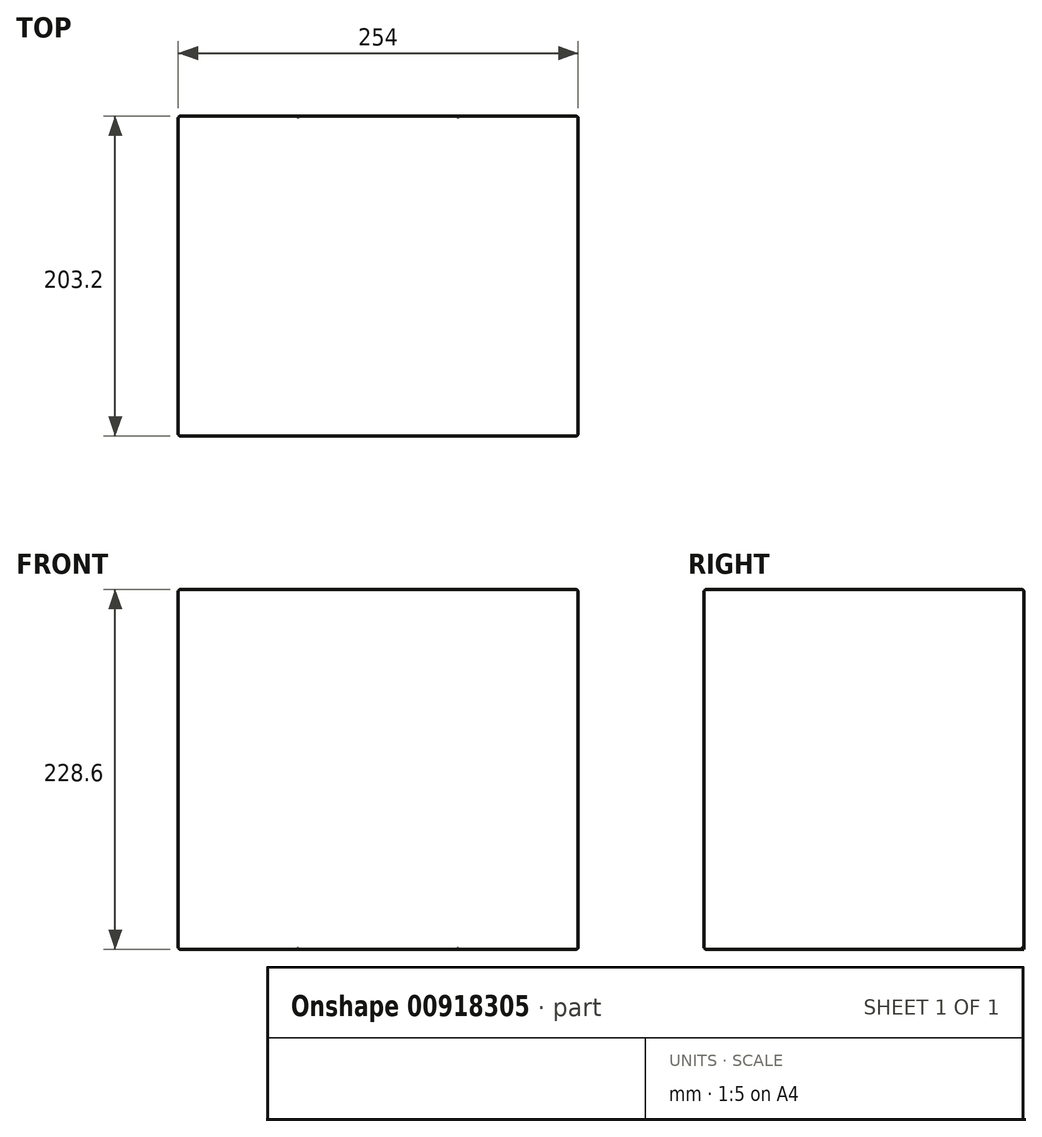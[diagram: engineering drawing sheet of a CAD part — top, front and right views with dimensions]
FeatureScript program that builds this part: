
annotation { "Feature Type Name" : "Feature", "Feature Type Description" : "" }
export const myFeature = defineFeature(function(context is Context, id is Id, definition is map)
    precondition{}
    {
        {
            var Q0;
            Q0=qCreatedBy(makeId("Front.planeOp"),FACE);
            var sketch = newSketch(context, id + "F0", { "sketchPlane" : qUnion([Q0])});
            skLineSegment(sketch, "E0.bottom", {"start": v(127, 114.3) * mm, "end": v(-127, 114.3) * mm});
            skLineSegment(sketch, "E0.top", {"start": v(127, -114.3) * mm, "end": v(-127, -114.3) * mm});
            skLineSegment(sketch, "E0.left", {"start": v(127, 114.3) * mm, "end": v(127, -114.3) * mm});
            skLineSegment(sketch, "E0.right", {"start": v(-127, 114.3) * mm, "end": v(-127, -114.3) * mm});
            skPoint(sketch, "E0.middle", {"position": v(0, 0) * mm});
            skSolve(sketch);
        }
        {
            var Q0;
            Q0=makeQuery(id+"F0.imprint","IMPRINT",FACE,{"disambiguationData":[TD([[makeQuery(id+"F0.imprint","IMPRINT",EDGE,{"derivedFrom":sQuery(id+"F0.wireOp",EDGE,"E0.bottom")}),1.0]])]});
            extrude(context, id + "F1", {"entities" : qUnion([Q0]), "endBound" : BoundingType.SYMMETRIC, "depth" : 203.2 * mm, "offsetDistance" : 25.4 * mm});
        }
        {
            var Q0;
            Q0=makeQuery(id+"F1.opExtrude","SWEPT_FACE",FACE,{"disambiguationData":[OSD([sQuery(id+"F0.wireOp",EDGE,"E0.top")])]});
            var sketch = newSketch(context, id + "F2", { "sketchPlane" : qUnion([Q0])});
            skLineSegment(sketch, "E1.bottom", {"start": v(127, -101.6) * mm, "end": v(50.8, -101.6) * mm});
            skLineSegment(sketch, "E1.top", {"start": v(127, 0) * mm, "end": v(50.8, 0) * mm});
            skLineSegment(sketch, "E1.left", {"start": v(127, -101.6) * mm, "end": v(127, 0) * mm});
            skLineSegment(sketch, "E1.right", {"start": v(50.8, -101.6) * mm, "end": v(50.8, 0) * mm});
            skLineSegment(sketch, "E2", {"start": v(0, -101.6) * mm, "end": v(0, 101.6) * mm, "construction": true});
            skLineSegment(sketch, "E3.MirrorCS", {"start": v(-127, 0) * mm, "end": v(-50.8, 0) * mm});
            skLineSegment(sketch, "E4.MirrorCS", {"start": v(-127, -101.6) * mm, "end": v(-127, 0) * mm});
            skLineSegment(sketch, "E5.MirrorCS", {"start": v(-50.8, -101.6) * mm, "end": v(-50.8, 0) * mm});
            skLineSegment(sketch, "E6.MirrorCS", {"start": v(-127, -101.6) * mm, "end": v(-50.8, -101.6) * mm});
            skSolve(sketch);
        }
        {
            var Q0;
            Q0=makeQuery(id+"F2.imprint","IMPRINT",FACE,{"disambiguationData":[TD([[makeQuery(id+"F2.imprint","IMPRINT",EDGE,{"derivedFrom":sQuery(id+"F2.wireOp",EDGE,"E1.bottom")}),-1.0]])]});
            var Q1;
            Q1=makeQuery(id+"F2.imprint","IMPRINT",FACE,{"disambiguationData":[TD([[makeQuery(id+"F2.imprint","IMPRINT",EDGE,{"derivedFrom":sQuery(id+"F2.wireOp",EDGE,"E3.MirrorCS")}),-1.0]])]});
            extrude(context, id + "F3", {"entities" : qUnion([Q0, Q1]), "operationType" : NewBodyOperationType.REMOVE, "oppositeDirection" : true, "depth" : 25.4 * mm, "offsetDistance" : 25.4 * mm});
        }
        {
            var Q0;
            Q0=makeQuery(id+"F3.boolean.opBoolean","COPY",FACE,{"derivedFrom":makeQuery(id+"F3.opExtrude","CAP_FACE",FACE,{"disambiguationData":[OSD([sQuery(id+"F2.wireOp",EDGE,"E1.bottom"),sQuery(id+"F2.wireOp",EDGE,"E1.top"),sQuery(id+"F2.wireOp",EDGE,"E1.left"),sQuery(id+"F2.wireOp",EDGE,"E1.right")])],"isStart":false})});
            var Q1;
            Q1=makeQuery(id+"F3.boolean.opBoolean","COPY",FACE,{"derivedFrom":makeQuery(id+"F3.opExtrude","CAP_FACE",FACE,{"disambiguationData":[OSD([sQuery(id+"F2.wireOp",EDGE,"E3.MirrorCS"),sQuery(id+"F2.wireOp",EDGE,"E4.MirrorCS"),sQuery(id+"F2.wireOp",EDGE,"E5.MirrorCS"),sQuery(id+"F2.wireOp",EDGE,"E6.MirrorCS")])],"isStart":false})});
            extrude(context, id + "F4", {"entities" : qUnion([Q0, Q1]), "depth" : 25.4 * mm, "offsetDistance" : 25.4 * mm});
        }
        {
            var Q0;
            Q0=makeQuery(id+"F1.opExtrude","CAP_FACE",FACE,{"disambiguationData":[OSD([sQuery(id+"F0.wireOp",EDGE,"E0.bottom"),sQuery(id+"F0.wireOp",EDGE,"E0.top"),sQuery(id+"F0.wireOp",EDGE,"E0.left"),sQuery(id+"F0.wireOp",EDGE,"E0.right")])],"isStart":false});
            var Q1;
            Q1=makeQuery(id+"F1.opExtrude","SWEPT_FACE",FACE,{"disambiguationData":[OSD([sQuery(id+"F0.wireOp",EDGE,"E0.bottom")])]});
            var Q2;
            Q2=makeQuery(id+"F1.opExtrude","CAP_EDGE",EDGE,{"disambiguationData":[OSD([sQuery(id+"F0.wireOp",EDGE,"E0.left")])],"isStart":true});
            var Q3;
            Q3=makeQuery(id+"F4.opExtrude","SWEPT_EDGE",EDGE,{"disambiguationData":[OSD([sQuery(id+"F2.wireOp",EDGE,"E1.bottom"),sQuery(id+"F2.wireOp",EDGE,"E1.left")])]});
            var Q4;
            Q4=makeQuery(id+"F1.opExtrude","CAP_EDGE",EDGE,{"disambiguationData":[OSD([sQuery(id+"F0.wireOp",EDGE,"E0.right")])],"isStart":true});
            var Q5;
            Q5=makeQuery(id+"F4.opExtrude","SWEPT_EDGE",EDGE,{"disambiguationData":[OSD([sQuery(id+"F2.wireOp",EDGE,"E4.MirrorCS"),sQuery(id+"F2.wireOp",EDGE,"E6.MirrorCS")])]});
            var Q6;
            Q6=makeQuery(id+"F1.opExtrude","SWEPT_EDGE",EDGE,{"disambiguationData":[OSD([sQuery(id+"F0.wireOp",EDGE,"E0.top"),sQuery(id+"F0.wireOp",EDGE,"E0.right")])]});
            var Q7;
            Q7=makeQuery(id+"F4.opExtrude","CAP_EDGE",EDGE,{"disambiguationData":[OSD([sQuery(id+"F2.wireOp",EDGE,"E4.MirrorCS")])],"isStart":false});
            var Q8;
            Q8=makeQuery(id+"F4.opExtrude","CAP_EDGE",EDGE,{"disambiguationData":[OSD([sQuery(id+"F2.wireOp",EDGE,"E6.MirrorCS")])],"isStart":false});
            var Q9;
            Q9=makeQuery(id+"F1.opExtrude","CAP_EDGE",EDGE,{"disambiguationData":[OSD([sQuery(id+"F0.wireOp",EDGE,"E0.top")])],"isStart":true});
            var Q10;
            Q10=makeQuery(id+"F4.opExtrude","CAP_EDGE",EDGE,{"disambiguationData":[OSD([sQuery(id+"F2.wireOp",EDGE,"E1.bottom")])],"isStart":false});
            var Q11;
            Q11=makeQuery(id+"F4.opExtrude","CAP_EDGE",EDGE,{"disambiguationData":[OSD([sQuery(id+"F2.wireOp",EDGE,"E1.left")])],"isStart":false});
            var Q12;
            Q12=makeQuery(id+"F1.opExtrude","SWEPT_EDGE",EDGE,{"disambiguationData":[OSD([sQuery(id+"F0.wireOp",EDGE,"E0.top"),sQuery(id+"F0.wireOp",EDGE,"E0.left")])]});
            fillet(context, id + "F5", {"entities" : qUnion([Q0, Q1, Q2, Q3, Q4, Q5, Q6, Q7, Q8, Q9, Q10, Q11, Q12]), "radius" : 1.52 * mm, "tangentPropagation" : true, "allowEdgeOverflow" : false});
        }
        {
            var Q0;
            Q0=makeQuery(id+"F1.opExtrude","SWEPT_FACE",FACE,{"disambiguationData":[OSD([sQuery(id+"F0.wireOp",EDGE,"E0.left")])]});
            var sketch = newSketch(context, id + "F6", { "sketchPlane" : qUnion([Q0])});
            skLineSegment(sketch, "E7.bottom", {"start": v(100.08, -88.9) * mm, "end": v(23.88, -88.9) * mm});
            skLineSegment(sketch, "E7.top", {"start": v(100.08, -63.5) * mm, "end": v(23.88, -63.5) * mm});
            skLineSegment(sketch, "E7.left", {"start": v(100.08, -88.9) * mm, "end": v(100.08, -63.5) * mm});
            skLineSegment(sketch, "E7.right", {"start": v(23.88, -88.9) * mm, "end": v(23.88, -63.5) * mm});
            skSolve(sketch);
        }
        {
            var Q0;
            Q0=makeQuery(id+"F6.imprint","IMPRINT",FACE,{"disambiguationData":[TD([[makeQuery(id+"F6.imprint","IMPRINT",EDGE,{"derivedFrom":sQuery(id+"F6.wireOp",EDGE,"E7.bottom")}),1.0]])]});
            extrude(context, id + "F7", {"entities" : qUnion([Q0]), "operationType" : NewBodyOperationType.REMOVE, "oppositeDirection" : true, "depth" : 25.4 * mm, "offsetDistance" : 25.4 * mm});
        }
        {
            var Q0;
            Q0=makeQuery(id+"F7.boolean.opBoolean","COPY",FACE,{"derivedFrom":makeQuery(id+"F7.opExtrude","CAP_FACE",FACE,{"disambiguationData":[OSD([sQuery(id+"F6.wireOp",EDGE,"E7.bottom"),sQuery(id+"F6.wireOp",EDGE,"E7.top"),sQuery(id+"F6.wireOp",EDGE,"E7.left"),sQuery(id+"F6.wireOp",EDGE,"E7.right")])],"isStart":false})});
            extrude(context, id + "F8", {"entities" : qUnion([Q0]), "operationType" : NewBodyOperationType.ADD, "depth" : 25.4 * mm, "offsetDistance" : 25.4 * mm});
        }
        {
            var Q0;
            Q0=makeQuery(id+"F1.opExtrude","SWEPT_FACE",FACE,{"disambiguationData":[OSD([sQuery(id+"F0.wireOp",EDGE,"E0.right")])]});
            var sketch = newSketch(context, id + "F9", { "sketchPlane" : qUnion([Q0])});
            skLineSegment(sketch, "E8.0", {"start": v(-100.08, -88.9) * mm, "end": v(-100.08, -63.5) * mm});
            skLineSegment(sketch, "E9.0", {"start": v(-100.08, -63.5) * mm, "end": v(-23.88, -63.5) * mm});
            skLineSegment(sketch, "E10.0", {"start": v(-100.08, -88.9) * mm, "end": v(-23.88, -88.9) * mm});
            skLineSegment(sketch, "E11.0", {"start": v(-23.88, -88.9) * mm, "end": v(-23.88, -63.5) * mm});
            skSolve(sketch);
        }
        {
            var Q0;
            Q0=makeQuery(id+"F9.imprint","IMPRINT",FACE,{"disambiguationData":[TD([[makeQuery(id+"F9.imprint","IMPRINT",EDGE,{"derivedFrom":sQuery(id+"F9.wireOp",EDGE,"E8.0")}),1.0]])]});
            extrude(context, id + "F10", {"entities" : qUnion([Q0]), "operationType" : NewBodyOperationType.REMOVE, "oppositeDirection" : true, "depth" : 25.4 * mm, "offsetDistance" : 25.4 * mm});
        }
        {
            var Q0;
            Q0=makeQuery(id+"F10.boolean.opBoolean","COPY",FACE,{"derivedFrom":makeQuery(id+"F10.opExtrude","CAP_FACE",FACE,{"disambiguationData":[OSD([sQuery(id+"F9.wireOp",EDGE,"E8.0"),sQuery(id+"F9.wireOp",EDGE,"E9.0"),sQuery(id+"F9.wireOp",EDGE,"E10.0"),sQuery(id+"F9.wireOp",EDGE,"E11.0")])],"isStart":false})});
            extrude(context, id + "F11", {"entities" : qUnion([Q0]), "operationType" : NewBodyOperationType.ADD, "depth" : 25.4 * mm, "offsetDistance" : 25.4 * mm});
        }
    });
